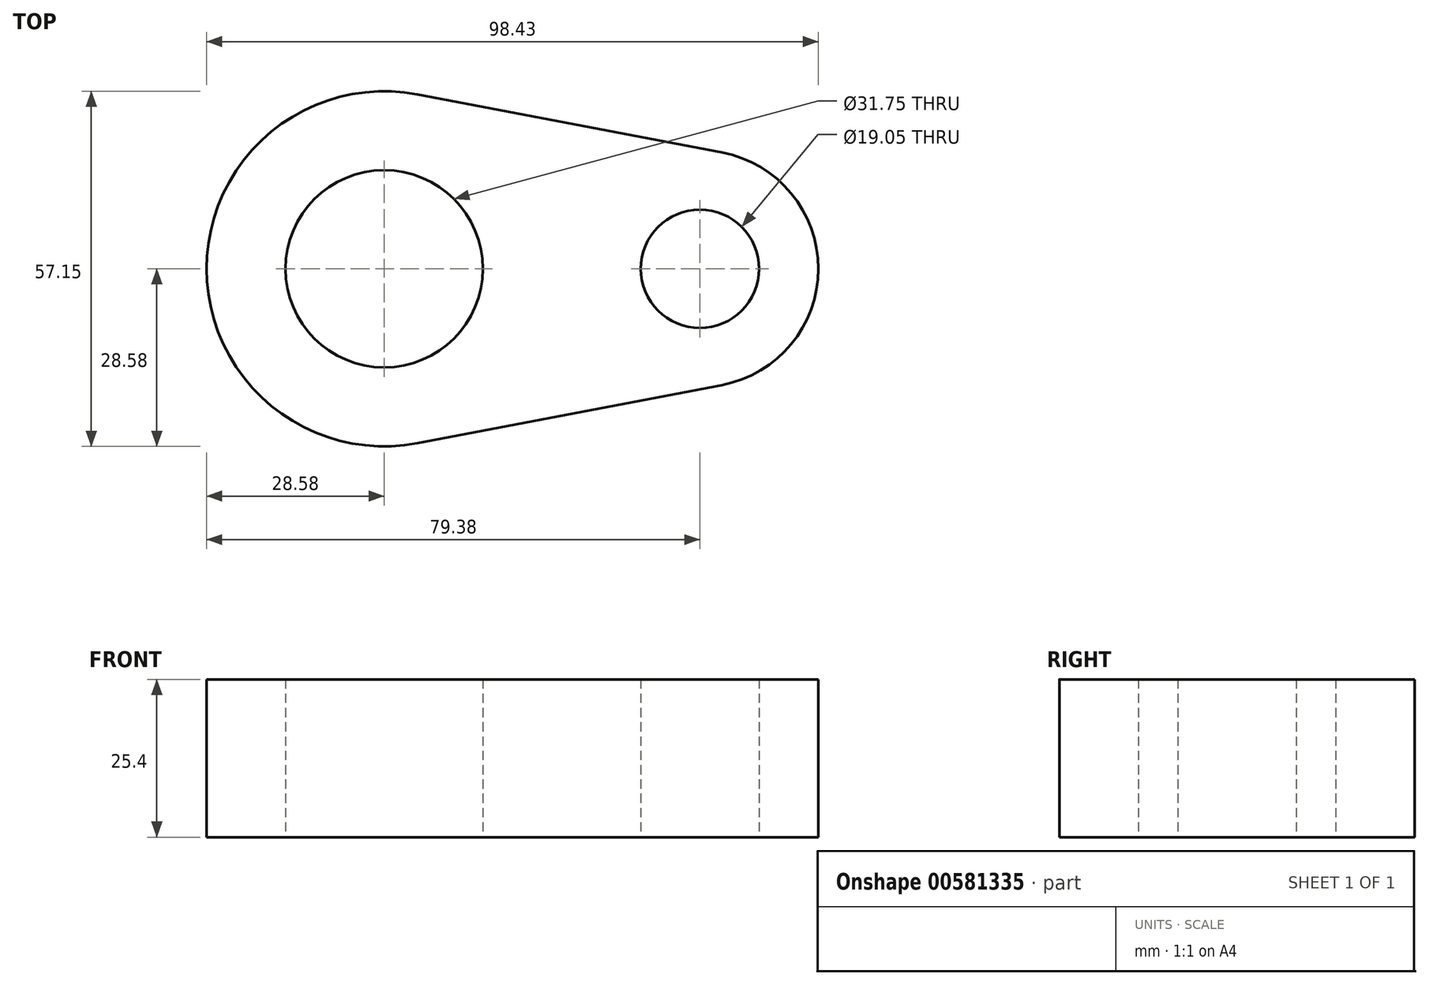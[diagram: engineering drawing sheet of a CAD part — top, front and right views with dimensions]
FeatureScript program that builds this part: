
annotation { "Feature Type Name" : "Feature", "Feature Type Description" : "" }
export const myFeature = defineFeature(function(context is Context, id is Id, definition is map)
    precondition{}
    {
        {
            var Q0;
            Q0=qCreatedBy(makeId("Top.planeOp"),FACE);
            var sketch = newSketch(context, id + "F0", { "sketchPlane" : qUnion([Q0])});
            skCircle(sketch, "E0", {"center": v(0, 0) * mm, "radius": 15.88 * mm});
            skCircle(sketch, "E1", {"center": v(0, 0) * mm, "radius": 28.58 * mm});
            skCircle(sketch, "E2", {"center": v(50.8, 0) * mm, "radius": 9.53 * mm});
            skCircle(sketch, "E3", {"center": v(50.8, 0) * mm, "radius": 19.05 * mm});
            skLineSegment(sketch, "E4", {"start": v(5.36, 28.07) * mm, "end": v(54.37, 18.71) * mm});
            skLineSegment(sketch, "E5", {"start": v(5.36, -28.07) * mm, "end": v(54.37, -18.71) * mm});
            skSolve(sketch);
        }
        {
            var Q0;
            Q0=makeQuery(id+"F0.imprint","IMPRINT",FACE,{"disambiguationData":[TD([[makeQuery(id+"F0.imprint","IMPRINT",EDGE,{"derivedFrom":sQuery(id+"F0.wireOp",EDGE,"E0")}),-1.0]])]});
            var Q1;
            Q1=makeQuery(id+"F0.imprint","IMPRINT",FACE,{"disambiguationData":[TD([[makeQuery(id+"F0.imprint","IMPRINT",EDGE,{"derivedFrom":sQuery(id+"F0.wireOp",EDGE,"E2")}),-1.0]])]});
            var Q2;
            {var subQ0=sQuery(id+"F0.wireOp",EDGE,"E4");Q2=makeQuery(id+"F0.imprint","IMPRINT",FACE,{"disambiguationData":[TD([[makeQuery(id+"F0.imprint","IMPRINT",EDGE,{"derivedFrom":subQ0}),-1.0]])]});}
            extrude(context, id + "F1", {"entities" : qUnion([Q0, Q1, Q2]), "depth" : 25.4 * mm, "offsetDistance" : 25.4 * mm});
        }
    });
